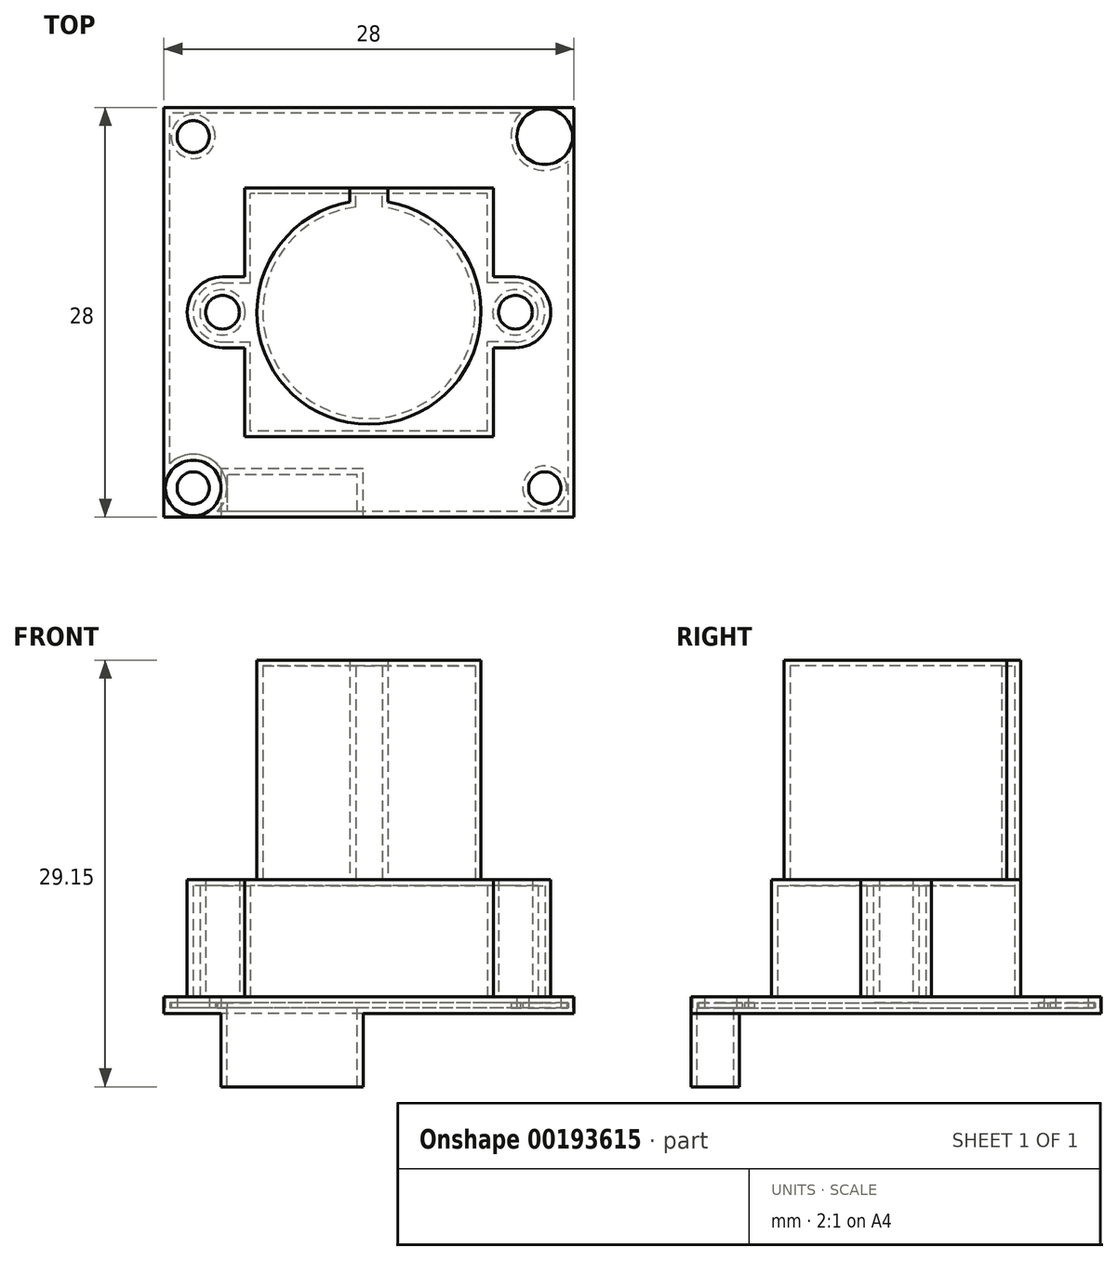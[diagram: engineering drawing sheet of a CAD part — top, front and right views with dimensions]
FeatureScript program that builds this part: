
annotation { "Feature Type Name" : "Feature", "Feature Type Description" : "" }
export const myFeature = defineFeature(function(context is Context, id is Id, definition is map)
    precondition{}
    {
        {
            var Q0;
            Q0=qCreatedBy(makeId("Top.planeOp"),FACE);
            var sketch = newSketch(context, id + "F0", { "sketchPlane" : qUnion([Q0])});
            skLineSegment(sketch, "E0.bottom", {"start": v(14, -14) * mm, "end": v(-14, -14) * mm});
            skLineSegment(sketch, "E0.top", {"start": v(14, 14) * mm, "end": v(-14, 14) * mm});
            skLineSegment(sketch, "E0.left", {"start": v(14, -14) * mm, "end": v(14, 14) * mm});
            skLineSegment(sketch, "E0.right", {"start": v(-14, -14) * mm, "end": v(-14, 14) * mm});
            skPoint(sketch, "E0.middle", {"position": v(0, 0) * mm});
            skLineSegment(sketch, "E1", {"start": v(0, 14) * mm, "end": v(0, -14) * mm, "construction": true});
            skLineSegment(sketch, "E2", {"start": v(-14, 0) * mm, "end": v(14, 0) * mm, "construction": true});
            skCircle(sketch, "E3", {"center": v(-12, 12) * mm, "radius": 1.1 * mm});
            skCircle(sketch, "E4", {"center": v(-12, 12) * mm, "radius": 1.9 * mm});
            skCircle(sketch, "E5.MirrorC", {"center": v(12, 12) * mm, "radius": 1.9 * mm});
            skCircle(sketch, "E6.MirrorC", {"center": v(12, 12) * mm, "radius": 1.1 * mm});
            skCircle(sketch, "E7.MirrorC", {"center": v(12, -12) * mm, "radius": 1.1 * mm});
            skCircle(sketch, "E8.MirrorC", {"center": v(12, -12) * mm, "radius": 1.9 * mm});
            skCircle(sketch, "E9.MirrorC", {"center": v(-12, -12) * mm, "radius": 1.1 * mm});
            skCircle(sketch, "E10.MirrorC", {"center": v(-12, -12) * mm, "radius": 1.9 * mm});
            skSolve(sketch);
        }
        {
            var Q0;
            Q0 = qSketchRegion(id + "F0", true);
            var Q1;
            Q1=makeQuery(id+"F0.imprint","IMPRINT",FACE,{"disambiguationData":[TD([[makeQuery(id+"F0.imprint","IMPRINT",EDGE,{"derivedFrom":sQuery(id+"F0.wireOp",EDGE,"E9.MirrorC")}),1.0]])]});
            var Q2;
            Q2=makeQuery(id+"F0.imprint","IMPRINT",FACE,{"disambiguationData":[TD([[makeQuery(id+"F0.imprint","IMPRINT",EDGE,{"derivedFrom":sQuery(id+"F0.wireOp",EDGE,"E7.MirrorC")}),-1.0]])]});
            var Q3;
            Q3=makeQuery(id+"F0.imprint","IMPRINT",FACE,{"disambiguationData":[TD([[makeQuery(id+"F0.imprint","IMPRINT",EDGE,{"derivedFrom":sQuery(id+"F0.wireOp",EDGE,"E3")}),-1.0]])]});
            var Q4;
            Q4=makeQuery(id+"F0.imprint","IMPRINT",FACE,{"disambiguationData":[TD([[makeQuery(id+"F0.imprint","IMPRINT",EDGE,{"derivedFrom":sQuery(id+"F0.wireOp",EDGE,"E5.MirrorC")}),-1.0]])]});
            extrude(context, id + "F1", {"entities" : qUnion([Q0, Q1, Q2, Q3, Q4]), "depth" : 1.15 * mm});
        }
        {
            var Q0;
            Q0=makeQuery(id+"F1.opExtrude","CAP_FACE",FACE,{"disambiguationData":[OSD([sQuery(id+"F0.wireOp",EDGE,"E0.bottom"),sQuery(id+"F0.wireOp",EDGE,"E0.top"),sQuery(id+"F0.wireOp",EDGE,"E0.left"),sQuery(id+"F0.wireOp",EDGE,"E0.right"),sQuery(id+"F0.wireOp",EDGE,"E3"),sQuery(id+"F0.wireOp",EDGE,"E6.MirrorC"),sQuery(id+"F0.wireOp",EDGE,"E7.MirrorC"),sQuery(id+"F0.wireOp",EDGE,"E9.MirrorC")])],"isStart":false});
            var sketch = newSketch(context, id + "F2", { "sketchPlane" : qUnion([Q0])});
            skLineSegment(sketch, "E11.0", {"start": v(0, 14) * mm, "end": v(0, -14) * mm, "construction": true});
            skLineSegment(sketch, "E11.1", {"start": v(-14, 0) * mm, "end": v(14, 0) * mm, "construction": true});
            skLineSegment(sketch, "E12.bottom", {"start": v(8.5, -8.5) * mm, "end": v(-8.5, -8.5) * mm});
            skLineSegment(sketch, "E12.top", {"start": v(8.5, 8.5) * mm, "end": v(-8.5, 8.5) * mm});
            skLineSegment(sketch, "E12.left", {"start": v(8.5, -8.5) * mm, "end": v(8.5, 8.5) * mm});
            skLineSegment(sketch, "E12.right", {"start": v(-8.5, -8.5) * mm, "end": v(-8.5, 8.5) * mm});
            skPoint(sketch, "E12.middle", {"position": v(0, 0) * mm});
            skCircle(sketch, "E13", {"center": v(-10, 0) * mm, "radius": 1.15 * mm});
            skCircle(sketch, "E14.MirrorC", {"center": v(10, 0) * mm, "radius": 1.15 * mm});
            skCircle(sketch, "E15", {"center": v(-10, 0) * mm, "radius": 2.42 * mm});
            skCircle(sketch, "E16.MirrorC", {"center": v(10, 0) * mm, "radius": 2.42 * mm});
            skLineSegment(sketch, "E17", {"start": v(-10, 2.42) * mm, "end": v(-8.5, 2.42) * mm});
            skLineSegment(sketch, "E18.MirrorCS", {"start": v(-10, -2.42) * mm, "end": v(-8.5, -2.42) * mm});
            skLineSegment(sketch, "E19.MirrorCS", {"start": v(10, 2.41) * mm, "end": v(8.5, 2.41) * mm});
            skLineSegment(sketch, "E20.MirrorCS", {"start": v(10, -2.42) * mm, "end": v(8.5, -2.42) * mm});
            skSolve(sketch);
        }
        {
            var Q0;
            Q0 = qSketchRegion(id + "F2", true);
            var Q1;
            {var subQ0=sQuery(id+"F2.wireOp",EDGE,"E15");var subQ1=sQuery(id+"F2.wireOp",EDGE,"E12.right");var subQ2=makeQuery(id+"F2.imprint","INTERSECT",VERTEX,{"disambiguationData":[OD(0.0)],"derivedFrom":[subQ1,subQ0]});Q1=makeQuery(id+"F2.imprint","IMPRINT",FACE,{"disambiguationData":[TD([[makeQuery(id+"F2.imprint","IMPRINT",EDGE,{"disambiguationData":[TD([[subQ2,-1.0]])],"derivedFrom":subQ1}),-1.0]])]});}
            var Q2;
            {var subQ0=sQuery(id+"F2.wireOp",EDGE,"E16.MirrorC");var subQ1=sQuery(id+"F2.wireOp",EDGE,"E12.left");var subQ2=makeQuery(id+"F2.imprint","INTERSECT",VERTEX,{"disambiguationData":[OD(0.0)],"derivedFrom":[subQ1,subQ0]});Q2=makeQuery(id+"F2.imprint","IMPRINT",FACE,{"disambiguationData":[TD([[makeQuery(id+"F2.imprint","IMPRINT",EDGE,{"disambiguationData":[TD([[subQ2,-1.0]])],"derivedFrom":subQ1}),1.0]])]});}
            extrude(context, id + "F3", {"entities" : qUnion([Q0, Q1, Q2]), "operationType" : NewBodyOperationType.ADD, "depth" : 8 * mm});
        }
        {
            var Q0;
            Q0=makeQuery(id+"F3.opExtrude","CAP_FACE",FACE,{"disambiguationData":[OSD([sQuery(id+"F2.wireOp",EDGE,"E12.bottom"),sQuery(id+"F2.wireOp",EDGE,"E12.top"),sQuery(id+"F2.wireOp",EDGE,"E12.left"),sQuery(id+"F2.wireOp",EDGE,"E12.right"),sQuery(id+"F2.wireOp",EDGE,"E13"),sQuery(id+"F2.wireOp",EDGE,"E14.MirrorC"),sQuery(id+"F2.wireOp",EDGE,"E15"),sQuery(id+"F2.wireOp",EDGE,"E16.MirrorC"),sQuery(id+"F2.wireOp",EDGE,"E17"),sQuery(id+"F2.wireOp",EDGE,"E18.MirrorCS"),sQuery(id+"F2.wireOp",EDGE,"E19.MirrorCS"),sQuery(id+"F2.wireOp",EDGE,"E20.MirrorCS")])],"isStart":false});
            var sketch = newSketch(context, id + "F4", { "sketchPlane" : qUnion([Q0])});
            skCircle(sketch, "E21", {"center": v(0, 0) * mm, "radius": 7.65 * mm});
            skLineSegment(sketch, "E22", {"start": v(-1.3, 7.54) * mm, "end": v(-1.3, 8.5) * mm});
            skLineSegment(sketch, "E23.MirrorCS", {"start": v(1.3, 7.54) * mm, "end": v(1.3, 8.5) * mm});
            skSolve(sketch);
        }
        {
            var Q0;
            Q0 = qSketchRegion(id + "F4", true);
            var Q1;
            {var subQ0=sQuery(id+"F4.wireOp",EDGE,"E22");Q1=makeQuery(id+"F4.imprint","IMPRINT",FACE,{"disambiguationData":[TD([[makeQuery(id+"F4.imprint","IMPRINT",EDGE,{"derivedFrom":subQ0}),-1.0]])]});}
            extrude(context, id + "F5", {"entities" : qUnion([Q0, Q1]), "operationType" : NewBodyOperationType.ADD, "depth" : 15 * mm});
        }
        {
            var Q0;
            Q0=makeQuery(id+"F0.imprint","IMPRINT",FACE,{"disambiguationData":[TD([[makeQuery(id+"F0.imprint","IMPRINT",EDGE,{"derivedFrom":sQuery(id+"F0.wireOp",EDGE,"E0.bottom")}),-1.0]])]});
            var sketch = newSketch(context, id + "F6", { "sketchPlane" : qUnion([Q0])});
            skLineSegment(sketch, "E24", {"start": v(-0.4, -14) * mm, "end": v(-0.4, -10.7) * mm});
            skLineSegment(sketch, "E25", {"start": v(-0.4, -10.7) * mm, "end": v(-10.1, -10.7) * mm});
            skLineSegment(sketch, "E26", {"start": v(-10.1, -10.7) * mm, "end": v(-10.1, -14) * mm});
            skSolve(sketch);
        }
        {
            var Q0;
            {var subQ5=sQuery(id+"F6.wireOp",EDGE,"E24");Q0=makeQuery(id+"F6.imprint","IMPRINT",FACE,{"disambiguationData":[TD([[makeQuery(id+"F6.imprint","IMPRINT",EDGE,{"derivedFrom":subQ5}),1.0]])]});}
            extrude(context, id + "F7", {"entities" : qUnion([Q0]), "operationType" : NewBodyOperationType.ADD, "oppositeDirection" : true, "depth" : 5 * mm});
        }
        {
            var Q0;
            Q0=makeQuery(id+"F7.opExtrude","CAP_FACE",FACE,{"disambiguationData":[OSD([sQuery(id+"F0.wireOp",EDGE,"E0.bottom"),sQuery(id+"F6.wireOp",EDGE,"E24"),sQuery(id+"F6.wireOp",EDGE,"E25"),sQuery(id+"F6.wireOp",EDGE,"E26")])],"isStart":false});
            shell(context, id + "F8", {"entities" : qUnion([Q0]), "thickness" : 0.4 * mm});
        }
    });
